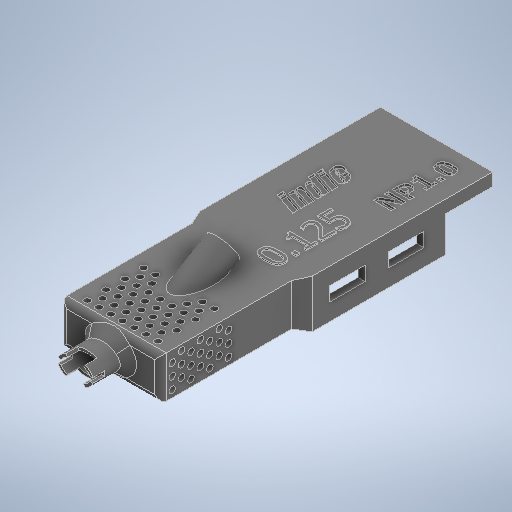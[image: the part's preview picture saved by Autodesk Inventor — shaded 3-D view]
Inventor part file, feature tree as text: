
AUTODESK INVENTOR PART (.ipt)
format: ipt  version: 2025 (Build 290162000, 162)  size: 1,469,952 bytes
history: native  units: in
note: dims shown in document units (in); Inventor stores cm internally (conversion verified against a paired STEP export)
features: extrude x18, reference x12, other x9, fillet x7, plane x4, sketch x3, chamfer x3, projected_geometry x2, loft x1, emboss x1
ambient origin geometry x8: Origin, YZ Plane, XZ Plane, XY Plane, X Axis, Y Axis, Z Axis, Center Point
bodies: Solid1 (feature_tree)
feature tree (60):
  extrude  "base_extrude"  Depth=0.02in
  extrude  "Extrusion4"  Depth=0.02in
  sketch  "Sketch for Plane"  dims[d7=0.02in d20=0.02in]
  plane  "Work Plane6"
  extrude  "screw_extrude"  Depth=0.0118in TaperAngle=0.0deg
  extrude  "screw_hole"  Depth=0.0118in
  extrude  "shank_cover"  Depth=0.0118in
  fillet  "Fillet1"  Radius=0.11in
  plane  "Work Plane14"
  other  "Work Point3"
  extrude  "top_extrude"  TaperAngle=60.0deg  [1 undecoded]
  loft  "base_to_top_loft"
  extrude  "close_base"  Depth=0.0118in TaperAngle=0.0deg
  extrude  "hole_for_shank"  Depth=0.0118in
  plane  "Work Plane16"
  plane  "Work Plane17"
  extrude  "cement_holes_1"  Depth=0.0118in TaperAngle=0.0deg
  extrude  "cement_holes_3"  Depth=0.0118in
  extrude  "cement_holes_2"  Depth=0.0118in TaperAngle=0.0deg
  extrude  "prongs"  Depth=0.0118in
  chamfer  "Chamfer16"  Distance=0.02in
  chamfer  "Chamfer17"  Distance=0.02in
  extrude  "cap_slots"  Depth=0.0118in
  extrude  "cap_slots_2"  Depth=0.0118in
  extrude  "top_chop"  Depth=0.0118in
  extrude  "cement_holes_4"  Depth=0.0118in TaperAngle=0.0deg
  chamfer  "skirt"  Angle=90.0deg  [1 undecoded]
  extrude  "Extrusion57"  TaperAngle=0.0deg  [1 undecoded]
  fillet  "Fillet8"  Radius=0.02in
  sketch  "sketch_for_dovetail_block"  dims[d21=0.4092in d22=0.0in d58=0.03in d59=0.0in d68=0.1885in d72=0.32in d73=0.11in d87=60.0deg d88=0.0984in d89=0.05in d90=0.0in d106=0.0335in d107=1.0in d108=0.0in d124=0.0591in d125=0.1181in d126=0.0in d152=0.0197in d157=0.02in d159=0.02in d197=0.0472in d199=0.02in d200=0.02in d201=0.02in d204=0.6043in d205=0.0in d206=0.0in d207=90.0deg d208=0.0in d209=90.0deg d210=0.02in d212=1.0in d213=0.0in d217=1.0in d218=0.0in d221=0.0394in d269=0.0217in d270=0.0315in d271=0.0394in d272=0.0394in d275=0.0315in d281=0.0217in d282=0.0394in d284=0.0197in d285=0.0394in d295=0.068in d304=0.0315in d305=0.0315in d306=0.0315in d307=0.0315in d310=0.0315in d312=0.0315in d313=0.0315in d328=0.0195in d334=0.0605in d335=0.0605in d338=0.3328in d339=0.1664in d340=0.0748in d341=0.0394in d342=0.0394in d343=0.0591in d344=0.0295in d345=0.0492in d354=1.0in d355=0.0in d358=0.0157in d359=0.0in d360=0.0157in d361=0.0in d381=0.0157in d382=0.1405in d383=0.0157in d384=0.0823in d385=0.3779in d386=0.0157in d387=0.1243in d388=0.1276in d389=0.0157in d390=0.3779in d391=0.0394in d392=0.0in d441=0.0394in d442=0.0079in d443=45.0deg d444=0.0079in d445=0.0394in d446=45.0deg d450=0.1181in d451=0.0472in d454=0.1614in d455=0.0807in d456=0.6043in d457=-0.0687in d458=1.0in d459=-0.0687in d474=0.1575in d475=0.0in d476=0.0591in d480=0.0777in d484=0.1614in d486=0.0394in d488=0.0787in d489=0.1614in d491=0.3363in d494=0.0025in d496=0.0049in d497=0.3937in d498=0.0in d501=0.0276in d502=0.0787in d503=45.0deg d505=0.1496in d506=0.0394in d507=0.0472in d508=0.0472in d509=0.0394in d510=0.0394in d511=0.3937in d512=0.0in d514=0.1575in d518=0.0118in d519=0.0in d522=0.0624in d523=0.0079in d524=0.0079in d525=0.0394in d526=0.0394in d527=0.0315in d528=0.0394in d529=0.0394in d530=0.0315in d531=0.0394in d532=0.0394in d533=0.0394in d534=0.0315in d535=0.0079in d536=0.0in d537=0.0039in d538=0.0in d539=0.1575in d540=0.1575in d541=0.0039in d542=0.0118in d8=0.0344in d9=0.5in d10=0.0344in d30=1.0in d31=1.0in d32=1.0in d33=0.15in d34=0.25in d35=0.375in d36=0.5635in d37=0.75in d38=0.8108in d39=0.0625in d40=0.75in d41=0.375in d43=1.0in d44=1.0in d45=1.0in d46=0.15in d47=0.25in d48=0.375in d49=0.5635in d50=0.75in d51=0.8108in d52=0.0625in d53=0.75in d54=0.375in d69=0.0344in d70=0.5in d71=0.0344in d78=0.5in d79=0.0344in d80=0.5in d81=0.0344in d109=0.5in d110=0.0344in d121=0.0in d122=0.0in d123=0.0in d127=0.0344in d153=0.5in d154=0.0344in d155=0.5in d156=0.0344in d181=0.5in d182=0.0344in d183=0.5in d184=0.0344in d192=0.5in d193=0.0344in d194=0.5in d195=0.0344in d196=0.5in d393=0.5in d394=0.0344in d395=0.5in d396=0.0344in d401=0.5in d402=0.0344in d403=0.5in d404=0.0344in d415=0.5in d416=0.0344in d417=0.5in d418=0.0344in d438=0.5in d439=0.0344in d440=0.5in d470=0.5in d471=0.0344in d472=0.5in d473=0.0344in d517=0.0197in d520=0.0344in d521=0.0in]
  extrude  "Extrusion59"  Depth=0.0118in TaperAngle=0.0deg
  fillet  "Fillet9"  Radius=1.0in
  emboss  "Emboss1"
  other  "tol_text"
  fillet  "Fillet10"  Radius=0.0394in
  fillet  "Fillet11"  Radius=0.0217in
  fillet  "Fillet12"  Radius=0.0315in
  fillet  "Fillet13"  Radius=0.0394in
  reference  "Reference7"
  reference  "Reference8"
  reference  "Reference9"
  reference  "Reference10"
  reference  "Reference11"
  reference  "Reference14"
  reference  "Reference15"
  reference  "Reference16"
  projected_geometry  "Projected Loop13"
  reference  "Reference23"
  reference  "Reference24"
  reference  "Reference25"
  reference  "Reference26"
  other  "Edges3"
  other  "Edges4"
  projected_geometry  "Projected Loop18"
  sketch  "Sketch77"  dims[d0=0.12in d3=0.02in]
  other  "text_sketch"
  parser-record x1  (decoder bookkeeping rows leaked as tree rows — omitted from the tree; the rows remain in map.json)
  other  "np1_full_assembly.iam"
  other  "NEUROPIXELS DOVE TAIL MOUNT:1"
  other  "NP2_FLEX_00-01:1"
note: 3 required parameter values undecoded (feature->parameter linkage not recoverable at this tier; creation-order binding heuristic only, values carry confidence <= 0.55)
note: 1 file-system path scrubbed to <path> (originals preserved in map.json)
